# Revit family: Trimless VPX124 Double Washer
name_source: partatom
category: Lighting Fixtures
revit_build: Autodesk Revit MEP 2014 (Build: 20130308_1515(x64)
units: mm (PartAtom-declared; Revit-internal decimal feet)

## types (1)
- Trimless VPX124 Double Washer
    Aperture (mm) = 104
    Apparent Load = 20 VA
    CRI = 80
    Color Filter = 16777215
    Colour temperature (K) = 27000/3000/3500/4000
    Cut Out (mm) = 140
    Description = Recessed low brightness LED Double Wallwasher
    Dimming Lamp Color Temperature Shift = <None>
    Height (mm) = 125
    Lamp = LED
    Luminous flux of luminaire (lm) = 2000
    Manufacturer = Designed Architectural Lighting
    Model = VPX124 Double Wallwasher
    O/A Diameter (mm) = 124
    Photometric Web File = C3908.ies
    Tilt Angle = 90.00°
    Type = Trimless VPX124 Double Wallwasher
    Type Comments = Recessed Trimless
    Wattage Comments = 19.5

## geometry (parser evidence)
native form markers: Sweep x1
no freeform markers — native parametric forms only
